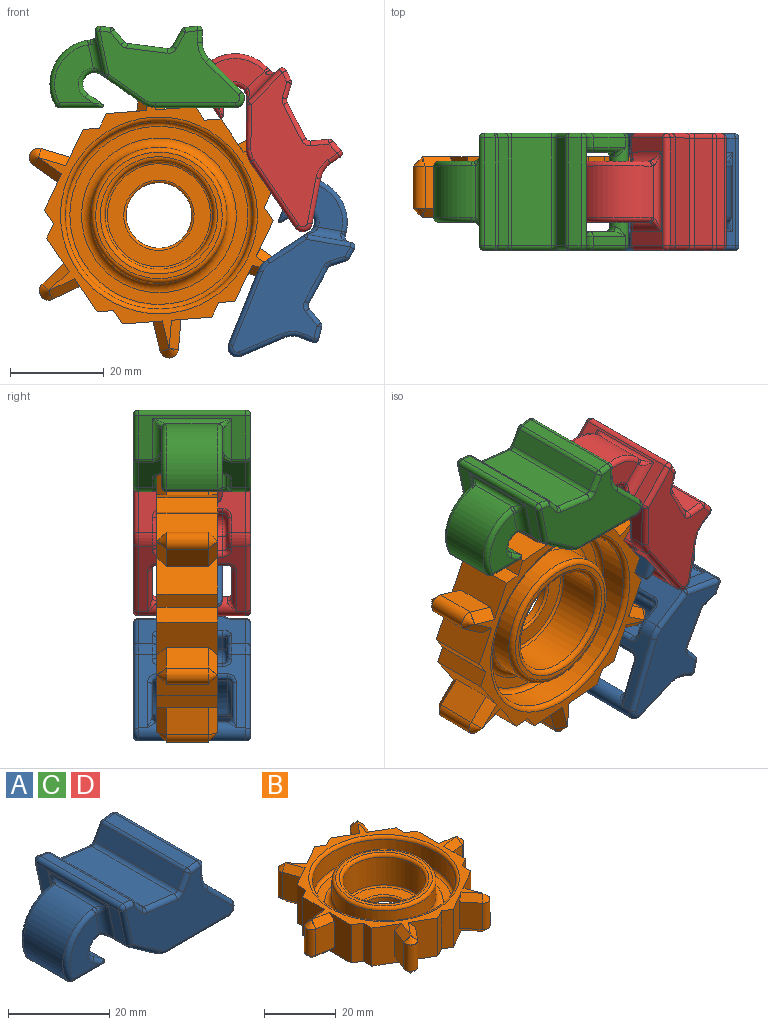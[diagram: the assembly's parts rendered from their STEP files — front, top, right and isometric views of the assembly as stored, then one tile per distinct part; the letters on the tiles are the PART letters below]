
ASSEMBLY  parts=4 mates=6
PART A: 153 faces, bbox 42.4x25x17.8 mm
  f0: plane 23x16.92mm, normal (0,0,-1), area 107.1mm2, adj f2,f8,f20,f39,f42,f43,f67,f75
  f1: plane 23x8.77mm, normal (-0.57,0,-0.82), area 148.5mm2, adj f2,f6,f39,f63,f96,f116,f119,f123
  f2: cylinder r=5mm len=3mm, axis (0,1,0), area 9.2mm2, adj f0,f1,f98,f112
  f3: plane 11x9.01mm, normal (0,0,-1), area 99.1mm2, adj f7,f36,f133,f145
  f4: cylinder r=9.5mm len=13.95mm, axis (0,1,0), area 208.4mm2, adj f35,f36,f130,f131,f142,f143
  f5: plane 11x3.18mm, normal (0.57,0,0.82), area 42.7mm2, adj f6,f7,f135,f147
  f6: cylinder r=2.5mm len=12.73mm, axis (0,1,0), area 87.9mm2, adj f1,f5,f136,f137,f148,f149
  f7: cylinder r=0.4mm len=11mm, axis (0,-1,0), area 11.1mm2, adj f3,f5,f134,f146
  f8: cylinder r=2mm len=23mm, axis (0,1,0), area 233.7mm2, adj f0,f22,f24,f44,f46,f48,f69,f74
  f9: cylinder r=11.5mm len=15mm, axis (0,1,0), area 163.9mm2, adj f20,f21,f45,f79,f81
  f10: plane 20.91x2.39mm, normal (1,0,-0.04), area 41.8mm2, adj f21,f30,f40,f50,f83,f103
  f11: plane 23x2.47mm, normal (1,0,0), area 56.9mm2, adj f30,f31,f70,f99
  f12: plane 23x2.65mm, normal (-0.13,0,0.99), area 61.4mm2, adj f31,f32,f66,f95
  f13: plane 23x3.44mm, normal (-0.87,0,0.48), area 90.5mm2, adj f32,f33,f62,f91
  f14: plane 23x8.59mm, normal (0.12,0,0.99), area 199.1mm2, adj f33,f34,f58,f87
  f15: plane 23x2.65mm, normal (0.77,0,0.64), area 79mm2, adj f34,f37,f54,f86
  f16: plane 23x2.27mm, normal (0.13,0,0.99), area 52.6mm2, adj f37,f38,f57,f90
  f17: plane 23x9.26mm, normal (-0.98,0,-0.2), area 65.2mm2, adj f28,f29,f35,f38,f61,f94,f139,f151
  f18: plane 29.85x15.42mm, normal (0,-1,0), area 269.5mm2, adj f54,f56,f57,f58,f60,f61,f62,f63
  f19: plane 29.85x15.42mm, normal (0,1,0), area 267.5mm2, adj f85,f86,f87,f89,f90,f91,f94,f95
  f20: cylinder r=1mm len=15mm, axis (0,1,0), area 24.8mm2, adj f0,f9,f43,f77
  f21: cylinder r=1mm len=16mm, axis (0,1,0), area 12.8mm2, adj f9,f10,f47,f51,f82
  f22: plane 7x6.94mm, normal (0.71,0,0.7), area 19.7mm2, adj f8,f41,f52,f71
  f23: plane 9.22x9.16mm, normal (0,1,0), area 55.1mm2, adj f42,f45,f46,f47,f52,f53
  f24: plane 6.81x6.51mm, normal (0.69,0,0.72), area 18.8mm2, adj f8,f40,f80,f104
  f25: plane 9.15x9mm, normal (0,-1,0), area 53.7mm2, adj f75,f76,f79,f80,f84
  f26: plane 12.4x8.23mm, normal (0,1,0), area 65.8mm2, adj f28,f143,f145,f147,f148
  f27: plane 12.4x8.23mm, normal (0,-1,0), area 65.8mm2, adj f29,f131,f133,f135,f136
  f28: cylinder r=2mm len=9.17mm, axis (0.2,0,-0.98), area 20.6mm2, adj f17,f26,f141,f142,f149,f150
  f29: cylinder r=2mm len=9.17mm, axis (-0.2,0,0.98), area 20.6mm2, adj f17,f27,f129,f130,f137,f138
  f30: cylinder r=1mm len=23mm, axis (0,1,0), area 0.8mm2, adj f10,f11,f41,f49,f72,f101
  f31: cylinder r=1mm len=23mm, axis (0,1,0), area 39.1mm2, adj f11,f12,f68,f97
  f32: cylinder r=1mm len=23mm, axis (0,-1,0), area 21.5mm2, adj f12,f13,f64,f93
  f33: cylinder r=1mm len=23mm, axis (0,-1,0), area 27.4mm2, adj f13,f14,f60,f89
  f34: cylinder r=1mm len=23mm, axis (0,-1,0), area 17.4mm2, adj f14,f15,f56,f85
  f35: cylinder r=1mm len=17mm, axis (0,1,0), area 23.1mm2, adj f4,f17,f129,f141
  f36: cylinder r=1mm len=11mm, axis (0,1,0), area 11.9mm2, adj f3,f4,f132,f144
  f37: cylinder r=1mm len=23mm, axis (0,1,0), area 17.2mm2, adj f15,f16,f55,f88
  f38: cylinder r=1mm len=23mm, axis (0,1,0), area 44mm2, adj f16,f17,f59,f92
  f39: cylinder r=5mm len=3mm, axis (0,1,0), area 9.2mm2, adj f0,f1,f65,f128
  f40: cylinder r=5mm len=3.81mm, axis (0,1,0), area 8.5mm2, adj f10,f24,f84,f105
  f41: cylinder r=5mm len=3.53mm, axis (0,1,0), area 7.8mm2, adj f22,f30,f53,f73
  f42: cylinder r=1mm len=10.45mm, axis (1,0,0), area 14.2mm2, adj f0,f23,f43,f44
  f43: bspline ~2.45x2.35mm, area 3.5mm2, adj f0,f20,f42,f45
  f44: bspline ~2.94x2mm, area 2.2mm2, adj f8,f42,f46
  f45: torus R=10.5mm, axis (0,-1,0), area 16.8mm2, adj f9,f23,f43,f47
  f46: torus R=3mm, axis (0,-1,0), area 5.5mm2, adj f8,f23,f44,f48
  f47: torus R=2mm, axis (0,-1,0), area 0.2mm2, adj f21,f23,f45,f51
  f48: bspline ~2.7x2mm, area 2.4mm2, adj f8,f46,f52
  f49: bspline ~0.28x0.27mm, area 0mm2, adj f30,f50,f53
  f50: bspline ~3.04x1.67mm, area 1.5mm2, adj f10,f49,f51,f53
  f51: bspline ~1.63x1.27mm, area 1.1mm2, adj f21,f47,f50,f53
  f52: cylinder r=1mm len=7.71mm, axis (0.7,0,-0.71), area 13.3mm2, adj f22,f23,f48,f53
  f53: torus R=6mm, axis (0,-1,0), area 2.9mm2, adj f23,f41,f49,f50,f51,f52
  f54: cylinder r=1mm len=3.29mm, axis (0.64,0,-0.77), area 5.4mm2, adj f15,f18,f55,f56
  f55: sphere r=1mm, area 0.7mm2, adj f37,f54,f57
  f56: torus R=2mm, axis (0,-1,0), area 1.6mm2, adj f18,f34,f54,f58
  f57: cylinder r=1mm len=2.4mm, axis (0.99,0,-0.13), area 3.6mm2, adj f16,f18,f55,f59
  f58: cylinder r=1mm len=8.71mm, axis (0.99,0,-0.12), area 13.6mm2, adj f14,f18,f56,f60
  f59: sphere r=1mm, area 1.9mm2, adj f38,f57,f61
  f60: torus R=2mm, axis (0,-1,0), area 2.5mm2, adj f18,f33,f58,f62
  f61: cylinder r=1mm len=9.46mm, axis (-0.2,0,0.98), area 14.9mm2, adj f17,f18,f59,f140
  f62: cylinder r=1mm len=3.93mm, axis (0.48,0,0.87), area 6.2mm2, adj f13,f18,f60,f64
  f63: cylinder r=1mm len=8.28mm, axis (-0.82,0,0.57), area 14.8mm2, adj f1,f18,f65,f140
  f64: sphere r=1mm, area 0.9mm2, adj f32,f62,f66
  f65: torus R=4mm, axis (0,-1,0), area 4.4mm2, adj f18,f39,f63,f67
  f66: cylinder r=1mm len=2.77mm, axis (0.99,0,0.13), area 4.2mm2, adj f12,f18,f64,f68
  f67: cylinder r=1mm len=16.92mm, axis (-1,0,0), area 26.6mm2, adj f0,f18,f65,f69
  f68: sphere r=1mm, area 1.7mm2, adj f31,f66,f70
  f69: torus R=1mm, axis (0,-1,0), area 6mm2, adj f8,f18,f67,f71
  f70: cylinder r=1mm len=2.47mm, axis (0,0,-1), area 3.9mm2, adj f11,f18,f68,f72
  f71: cylinder r=1mm len=7.71mm, axis (-0.7,0,0.71), area 15.5mm2, adj f18,f22,f69,f73
  f72: sphere r=1mm, area 0mm2, adj f30,f70,f73
  f73: torus R=6mm, axis (0,-1,0), area 6.6mm2, adj f18,f41,f71,f72
  f74: bspline ~2.94x2mm, area 2.2mm2, adj f8,f75,f76
  f75: cylinder r=1mm len=10.45mm, axis (-1,0,0), area 14.2mm2, adj f0,f25,f74,f77
  f76: torus R=3mm, axis (0,1,0), area 5.4mm2, adj f8,f25,f74,f78
  f77: bspline ~2.46x2.35mm, area 3.5mm2, adj f0,f20,f75,f79
  f78: bspline ~2.94x2mm, area 2.4mm2, adj f8,f76,f80
  f79: torus R=10.5mm, axis (0,1,0), area 16.7mm2, adj f9,f25,f77,f81
  f80: cylinder r=1mm len=7.5mm, axis (-0.72,0,0.69), area 12.6mm2, adj f24,f25,f78,f84
  f81: bspline ~1x0.87mm, area 0mm2, adj f9,f79,f82,f84
  f82: bspline ~1.72x1.35mm, area 1.2mm2, adj f21,f81,f83,f84
  f83: bspline ~2.91x1.56mm, area 0.8mm2, adj f10,f82,f84
  f84: torus R=6mm, axis (0,1,0), area 3.3mm2, adj f25,f40,f80,f81,f82,f83
  f85: torus R=2mm, axis (0,-1,0), area 1.6mm2, adj f19,f34,f86,f87
  f86: cylinder r=1mm len=3.29mm, axis (-0.64,0,0.77), area 5.4mm2, adj f15,f19,f85,f88
  f87: cylinder r=1mm len=8.71mm, axis (-0.99,0,0.12), area 13.6mm2, adj f14,f19,f85,f89
  f88: sphere r=1mm, area 0.7mm2, adj f37,f86,f90
  f89: torus R=2mm, axis (0,-1,0), area 2.5mm2, adj f19,f33,f87,f91
  f90: cylinder r=1mm len=2.4mm, axis (-0.99,0,0.13), area 3.6mm2, adj f16,f19,f88,f92
  f91: cylinder r=1mm len=3.93mm, axis (-0.48,0,-0.87), area 6.2mm2, adj f13,f19,f89,f93
  f92: sphere r=1mm, area 1.9mm2, adj f38,f90,f94
  f93: sphere r=1mm, area 0.9mm2, adj f32,f91,f95
  f94: cylinder r=1mm len=9.46mm, axis (0.2,0,-0.98), area 14.9mm2, adj f17,f19,f92,f152
  f95: cylinder r=1mm len=2.77mm, axis (-0.99,0,-0.13), area 4.2mm2, adj f12,f19,f93,f97
  f96: cylinder r=1mm len=8.28mm, axis (0.82,0,-0.57), area 14.8mm2, adj f1,f19,f98,f152
  f97: sphere r=1mm, area 1.7mm2, adj f31,f95,f99
  f98: torus R=4mm, axis (0,-1,0), area 4.4mm2, adj f2,f19,f96,f100
  f99: cylinder r=1mm len=2.47mm, axis (0,0,1), area 3.9mm2, adj f11,f19,f97,f101
  f100: cylinder r=1mm len=16.92mm, axis (1,0,0), area 26.6mm2, adj f0,f19,f98,f102
  f101: sphere r=1mm, area 0mm2, adj f30,f99,f103
  f102: torus R=1mm, axis (0,-1,0), area 6.1mm2, adj f8,f19,f100,f104
  f103: cylinder r=1mm len=1mm, axis (0.04,0,1), area 0.2mm2, adj f10,f19,f101,f105
  f104: cylinder r=1mm len=7.5mm, axis (-0.72,0,0.69), area 14.8mm2, adj f19,f24,f102,f105
  f105: torus R=6mm, axis (0,-1,0), area 7.1mm2, adj f19,f40,f103,f104
  f106: plane 13x4.76mm, normal (-1,0,-0.08), area 62mm2, adj f107,f114,f120,f121
  f107: cylinder r=3mm len=13mm, axis (0,-1,0), area 99.1mm2, adj f106,f108,f111,f118
  f108: plane 13x2.71mm, normal (0.87,0,-0.49), area 40.5mm2, adj f107,f115,f122,f123
  f109: plane 6.42x5.75mm, normal (0,-1,0), area 25.2mm2, adj f111,f112,f113,f114,f115,f116
  f110: plane 6.42x5.75mm, normal (0,1,0), area 25.2mm2, adj f118,f121,f122,f126,f127,f128
  f111: torus R=2mm, axis (0,-1,0), area 10.5mm2, adj f107,f109,f114,f115
  f112: torus R=4mm, axis (0,-1,0), area 4.4mm2, adj f2,f109,f113,f116
  f113: cylinder r=1mm len=1mm, axis (-1,0,0), area 1.4mm2, adj f0,f109,f112,f117
  f114: cylinder r=1mm len=4.84mm, axis (-0.08,0,1), area 7.4mm2, adj f106,f109,f111,f117
  f115: cylinder r=1mm len=3.37mm, axis (-0.49,0,-0.87), area 5mm2, adj f108,f109,f111,f119
  f116: cylinder r=1mm len=3.16mm, axis (-0.82,0,0.57), area 5mm2, adj f1,f109,f112,f119
  f117: bspline ~2.36x2.09mm, area 3.3mm2, adj f0,f113,f114,f120
  f118: torus R=2mm, axis (0,-1,0), area 10.5mm2, adj f107,f110,f121,f122
  f119: bspline ~2.22x2mm, area 3.5mm2, adj f1,f115,f116,f123
  f120: cylinder r=1mm len=13mm, axis (0,1,0), area 19.3mm2, adj f0,f106,f117,f124
  f121: cylinder r=1mm len=4.84mm, axis (0.08,0,-1), area 7.4mm2, adj f106,f110,f118,f124
  f122: cylinder r=1mm len=3.37mm, axis (0.49,0,0.87), area 5mm2, adj f108,f110,f118,f125
  f123: cylinder r=1mm len=13mm, axis (0,-1,0), area 21.6mm2, adj f1,f108,f119,f125
  f124: bspline ~2.36x2mm, area 3.3mm2, adj f0,f120,f121,f126
  f125: bspline ~2.22x2.2mm, area 3.5mm2, adj f1,f122,f123,f127
  f126: cylinder r=1mm len=1mm, axis (1,0,0), area 1.4mm2, adj f0,f110,f124,f128
  f127: cylinder r=1mm len=3.16mm, axis (0.82,0,-0.57), area 5mm2, adj f1,f110,f125,f128
  f128: torus R=4mm, axis (0,-1,0), area 4.4mm2, adj f39,f110,f126,f127
  f129: bspline ~2.98x2.25mm, area 2.6mm2, adj f29,f35,f130
  f130: bspline ~2.24x1.31mm, area 1mm2, adj f4,f29,f129,f131
  f131: torus R=8.5mm, axis (0,-1,0), area 27.4mm2, adj f4,f27,f130,f132
  f132: sphere r=1mm, area 1.1mm2, adj f36,f131,f133
  f133: cylinder r=1mm len=9.01mm, axis (1,0,0), area 13.1mm2, adj f3,f27,f132,f134
  f134: bspline ~3.17x1.59mm, area 1.4mm2, adj f7,f133,f135
  f135: cylinder r=1mm len=3.75mm, axis (0.82,0,-0.57), area 5mm2, adj f5,f27,f134,f136
  f136: torus R=3.5mm, axis (0,-1,0), area 11mm2, adj f6,f27,f135,f137
  f137: bspline ~2.5x1.99mm, area 2.4mm2, adj f6,f29,f136,f138
  f138: bspline ~2.14x1.42mm, area 1.9mm2, adj f1,f29,f137,f139
  f139: cylinder r=1mm len=3mm, axis (0,1,0), area 2.3mm2, adj f1,f17,f138,f140
  f140: sphere r=1mm, area 0.8mm2, adj f61,f63,f139
  f141: bspline ~2.98x2.25mm, area 2.3mm2, adj f28,f35,f142
  f142: bspline ~2.24x1.31mm, area 1mm2, adj f4,f28,f141,f143
  f143: torus R=8.5mm, axis (0,-1,0), area 27.4mm2, adj f4,f26,f142,f144
  f144: sphere r=1mm, area 1.1mm2, adj f36,f143,f145
  f145: cylinder r=1mm len=9.01mm, axis (-1,0,0), area 13.1mm2, adj f3,f26,f144,f146
  f146: bspline ~3.17x1.16mm, area 1.4mm2, adj f7,f145,f147
  f147: cylinder r=1mm len=3.75mm, axis (-0.82,0,0.57), area 5mm2, adj f5,f26,f146,f148
  f148: torus R=3.5mm, axis (0,-1,0), area 11mm2, adj f6,f26,f147,f149
  f149: bspline ~2.5x1.99mm, area 2.4mm2, adj f6,f28,f148,f150
  f150: bspline ~2.14x1.42mm, area 1.9mm2, adj f1,f28,f149,f151
  f151: cylinder r=1mm len=3mm, axis (0,1,0), area 2.3mm2, adj f1,f17,f150,f152
  f152: sphere r=1mm, area 0.8mm2, adj f94,f96,f151
PART B: 94 faces, bbox 61x53.4x13 mm
  f0: cylinder r=7mm len=14mm, axis (0,0,-1), area 66mm2, adj f9,f56
  f1: plane 13x3mm, normal (-0.5,0.87,0), area 45mm2, adj f7,f8,f9,f11
  f2: plane 13x3.46mm, normal (1,0,0), area 45mm2, adj f3,f8,f9,f38
  f3: plane 13x7.42mm, normal (0.5,0.87,0), area 89mm2, adj f2,f4,f8,f9,f66,f69
  f4: plane 9x5.99mm, normal (0.93,-0.35,0), area 57.6mm2, adj f3,f5,f66,f69
  f5: cylinder r=2mm len=9mm, axis (0,0,-1), area 50.8mm2, adj f4,f6,f65,f68
  f6: plane 9x4.96mm, normal (-0.77,0.63,0), area 57.6mm2, adj f5,f7,f64,f67
  f7: plane 13x7.42mm, normal (0.5,0.87,0), area 89mm2, adj f1,f6,f8,f9,f64,f67
  f8: plane 57.03x49.39mm, normal (0,0,1), area 343.6mm2, adj f1,f2,f3,f7,f10,f11,f12,f16
  f9: plane 57.03x49.39mm, normal (0,0,-1), area 1575.1mm2, adj f0,f1,f2,f3,f7,f10,f11,f12
  f10: plane 13x3.46mm, normal (-1,0,0), area 45mm2, adj f8,f9,f16,f18
  f11: plane 13x3mm, normal (0.5,0.87,0), area 45mm2, adj f1,f8,f9,f12
  f12: plane 13x7.42mm, normal (-0.5,0.87,0), area 89mm2, adj f8,f9,f11,f13,f60,f63
  f13: plane 9x4.96mm, normal (0.77,0.63,0), area 57.6mm2, adj f12,f14,f60,f63
  f14: cylinder r=2mm len=9mm, axis (0,0,-1), area 50.8mm2, adj f13,f15,f59,f62
  f15: plane 9x5.99mm, normal (-0.93,-0.35,0), area 57.6mm2, adj f14,f16,f58,f61
  f16: plane 13x7.42mm, normal (-0.5,0.87,0), area 89mm2, adj f8,f9,f10,f15,f58,f61
  f17: plane 13x3mm, normal (-0.5,-0.87,0), area 45mm2, adj f8,f9,f23,f25
  f18: plane 13x3mm, normal (-0.5,0.87,0), area 45mm2, adj f8,f9,f10,f19
  f19: plane 13x8.56mm, normal (-1,0,0), area 89mm2, adj f8,f9,f18,f20,f78,f81
  f20: plane 9x6.32mm, normal (-0.16,0.99,0), area 57.6mm2, adj f19,f21,f78,f81
  f21: cylinder r=2mm len=9mm, axis (0,0,-1), area 50.8mm2, adj f20,f22,f77,f80
  f22: plane 9x6.32mm, normal (-0.16,-0.99,0), area 57.6mm2, adj f21,f23,f76,f79
  f23: plane 13x8.56mm, normal (-1,0,0), area 89mm2, adj f8,f9,f17,f22,f76,f79
  f24: plane 13x3mm, normal (0.5,-0.87,0), area 45mm2, adj f8,f9,f30,f32
  f25: plane 13x3.46mm, normal (-1,0,0), area 45mm2, adj f8,f9,f17,f26
  f26: plane 13x7.42mm, normal (-0.5,-0.87,0), area 89mm2, adj f8,f9,f25,f27,f84,f87
  f27: plane 9x5.99mm, normal (-0.93,0.35,0), area 57.6mm2, adj f26,f28,f84,f87
  f28: cylinder r=2mm len=9mm, axis (0,0,-1), area 50.8mm2, adj f27,f29,f83,f86
  f29: plane 9x4.96mm, normal (0.77,-0.63,0), area 57.6mm2, adj f28,f30,f82,f85
  f30: plane 13x7.42mm, normal (-0.5,-0.87,0), area 89mm2, adj f8,f9,f24,f29,f82,f85
  f31: plane 13x3.46mm, normal (1,0,0), area 45mm2, adj f8,f9,f37,f39
  f32: plane 13x3mm, normal (-0.5,-0.87,0), area 45mm2, adj f8,f9,f24,f33
  f33: plane 13x7.42mm, normal (0.5,-0.87,0), area 89mm2, adj f8,f9,f32,f34,f90,f93
  f34: plane 9x4.96mm, normal (-0.77,-0.63,0), area 57.6mm2, adj f33,f35,f90,f93
  f35: cylinder r=2mm len=9mm, axis (0,0,-1), area 50.8mm2, adj f34,f36,f89,f92
  f36: plane 9x5.99mm, normal (0.93,0.35,0), area 57.6mm2, adj f35,f37,f88,f91
  f37: plane 13x7.42mm, normal (0.5,-0.87,0), area 89mm2, adj f8,f9,f31,f36,f88,f91
  f38: plane 13x3mm, normal (0.5,0.87,0), area 45mm2, adj f2,f8,f9,f44
  f39: plane 13x3mm, normal (0.5,-0.87,0), area 45mm2, adj f8,f9,f31,f40
  f40: plane 13x8.56mm, normal (1,0,0), area 89mm2, adj f8,f9,f39,f41,f72,f75
  f41: plane 9x6.32mm, normal (0.16,-0.99,0), area 57.6mm2, adj f40,f42,f72,f75
  f42: cylinder r=2mm len=9mm, axis (0,0,-1), area 50.8mm2, adj f41,f43,f71,f74
  f43: plane 9x6.32mm, normal (0.16,0.99,0), area 57.6mm2, adj f42,f44,f70,f73
  f44: plane 13x8.56mm, normal (1,0,0), area 89mm2, adj f8,f9,f38,f43,f70,f73
  f45: cylinder r=20mm len=40mm, axis (0,0,1), area 754mm2, adj f47,f48
  f46: plane 38x38mm, normal (0,0,1), area 278.8mm2, adj f48,f55
  f47: torus R=21mm, axis (0,0,1), area 201mm2, adj f8,f45
  f48: torus R=19mm, axis (0,0,1), area 193.8mm2, adj f45,f46
  f49: cylinder r=11.5mm len=23mm, axis (0,0,-1), area 686.4mm2, adj f53,f57
  f50: cylinder r=14.5mm len=29mm, axis (0,0,-1), area 455.5mm2, adj f54,f55
  f51: plane 27x27mm, normal (0,0,1), area 81.7mm2, adj f53,f54
  f52: plane 22x22mm, normal (0,0,1), area 203.4mm2, adj f56,f57
  f53: torus R=12.5mm, axis (0,0,1), area 117.1mm2, adj f49,f51
  f54: torus R=13.5mm, axis (0,0,1), area 139.5mm2, adj f50,f51
  f55: torus R=16.5mm, axis (0,0,1), area 300.6mm2, adj f46,f50
  f56: torus R=7.5mm, axis (0,0,1), area 35.4mm2, adj f0,f52
  f57: torus R=11mm, axis (0,0,1), area 55.9mm2, adj f49,f52
  f58: plane 6.7x4.03mm, normal (-0.66,-0.25,0.71), area 17.7mm2, adj f8,f15,f16,f59
  f59: cone r=2mm half-angle=45deg, axis (0,0,-1), area 8mm2, adj f14,f58,f60
  f60: plane 5.97x5.6mm, normal (0.55,0.45,0.71), area 17.7mm2, adj f8,f12,f13,f59
  f61: plane 6.7x4.03mm, normal (-0.66,-0.25,-0.71), area 17.7mm2, adj f9,f15,f16,f62
  f62: cone r=2mm half-angle=45deg, axis (0,0,1), area 8mm2, adj f14,f61,f63
  f63: plane 5.97x5.6mm, normal (0.55,0.45,-0.71), area 17.7mm2, adj f9,f12,f13,f62
  f64: plane 5.97x5.6mm, normal (-0.55,0.45,0.71), area 17.7mm2, adj f6,f7,f8,f65
  f65: cone r=2mm half-angle=45deg, axis (0,0,-1), area 8mm2, adj f5,f64,f66
  f66: plane 6.7x4.03mm, normal (0.66,-0.25,0.71), area 17.7mm2, adj f3,f4,f8,f65
  f67: plane 5.97x5.6mm, normal (-0.55,0.45,-0.71), area 17.7mm2, adj f6,f7,f9,f68
  f68: cone r=2mm half-angle=45deg, axis (0,0,1), area 8mm2, adj f5,f67,f69
  f69: plane 6.7x4.03mm, normal (0.66,-0.25,-0.71), area 17.7mm2, adj f3,f4,f9,f68
  f70: plane 6.32x3mm, normal (0.11,0.7,0.71), area 17.7mm2, adj f8,f43,f44,f71
  f71: cone r=2mm half-angle=45deg, axis (0,0,-1), area 8mm2, adj f42,f70,f72
  f72: plane 6.32x3mm, normal (0.11,-0.7,0.71), area 17.7mm2, adj f8,f40,f41,f71
  f73: plane 6.32x3mm, normal (0.11,0.7,-0.71), area 17.7mm2, adj f9,f43,f44,f74
  f74: cone r=2mm half-angle=45deg, axis (0,0,1), area 8mm2, adj f42,f73,f75
  f75: plane 6.32x3mm, normal (0.11,-0.7,-0.71), area 17.7mm2, adj f9,f40,f41,f74
  f76: plane 6.32x3mm, normal (-0.11,-0.7,0.71), area 17.7mm2, adj f8,f22,f23,f77
  f77: cone r=2mm half-angle=45deg, axis (0,0,-1), area 8mm2, adj f21,f76,f78
  f78: plane 6.32x3mm, normal (-0.11,0.7,0.71), area 17.7mm2, adj f8,f19,f20,f77
  f79: plane 6.32x3mm, normal (-0.11,-0.7,-0.71), area 17.7mm2, adj f9,f22,f23,f80
  f80: cone r=2mm half-angle=45deg, axis (0,0,1), area 8mm2, adj f21,f79,f81
  f81: plane 6.32x3mm, normal (-0.11,0.7,-0.71), area 17.7mm2, adj f9,f19,f20,f80
  f82: plane 5.97x5.6mm, normal (0.55,-0.45,0.71), area 17.7mm2, adj f8,f29,f30,f83
  f83: cone r=2mm half-angle=45deg, axis (0,0,-1), area 8mm2, adj f28,f82,f84
  f84: plane 6.7x4.03mm, normal (-0.66,0.25,0.71), area 17.7mm2, adj f8,f26,f27,f83
  f85: plane 5.97x5.6mm, normal (0.55,-0.45,-0.71), area 17.7mm2, adj f9,f29,f30,f86
  f86: cone r=2mm half-angle=45deg, axis (0,0,1), area 8mm2, adj f28,f85,f87
  f87: plane 6.7x4.03mm, normal (-0.66,0.25,-0.71), area 17.7mm2, adj f9,f26,f27,f86
  f88: plane 6.7x4.03mm, normal (0.66,0.25,0.71), area 17.7mm2, adj f8,f36,f37,f89
  f89: cone r=2mm half-angle=45deg, axis (0,0,-1), area 8mm2, adj f35,f88,f90
  f90: plane 5.97x5.6mm, normal (-0.55,-0.45,0.71), area 17.7mm2, adj f8,f33,f34,f89
  f91: plane 6.7x4.03mm, normal (0.66,0.25,-0.71), area 17.7mm2, adj f9,f36,f37,f92
  f92: cone r=2mm half-angle=45deg, axis (0,0,1), area 8mm2, adj f35,f91,f93
  f93: plane 5.97x5.6mm, normal (-0.55,-0.45,-0.71), area 17.7mm2, adj f9,f33,f34,f92
PART C: same geometry as A
PART D: same geometry as A
PLACE A rot(axis=(0,1,0),111.8deg) t=(46.79,39.27,-24.07)mm
PLACE B rot(axis=(0.95,0.22,-0.22),92.8deg) t=(12.55,34.27,-31.43)mm
PLACE C t=(-10.71,39.27,-3.43)mm fixed
PLACE D rot(axis=(0,1,0),55.6deg) t=(23.43,39.27,1.41)mm fixed
MATE planar C.f18 <-> D.f18  axis (0,-1,0) through (14.37,14.27,-1.06)mm
MATE planar B.f0 <-> C.f109  axis (0,1,0) through (12.55,34.27,-31.43)mm
MATE planar B.f7 <-> D.f0  axis (0.83,0,0.56) through (27.7,27.77,-13.69)mm
MATE planar D.f18 <-> A.f18  axis (0,-1,0) through (39.54,14.27,-17.95)mm
MATE cylindrical D.f8 <-> A.f4  axis (0,1,0) through (43.25,26.77,-32.89)mm
MATE cylindrical D.f4 <-> C.f8  axis (0,1,0) through (28.79,26.77,-6.43)mm
